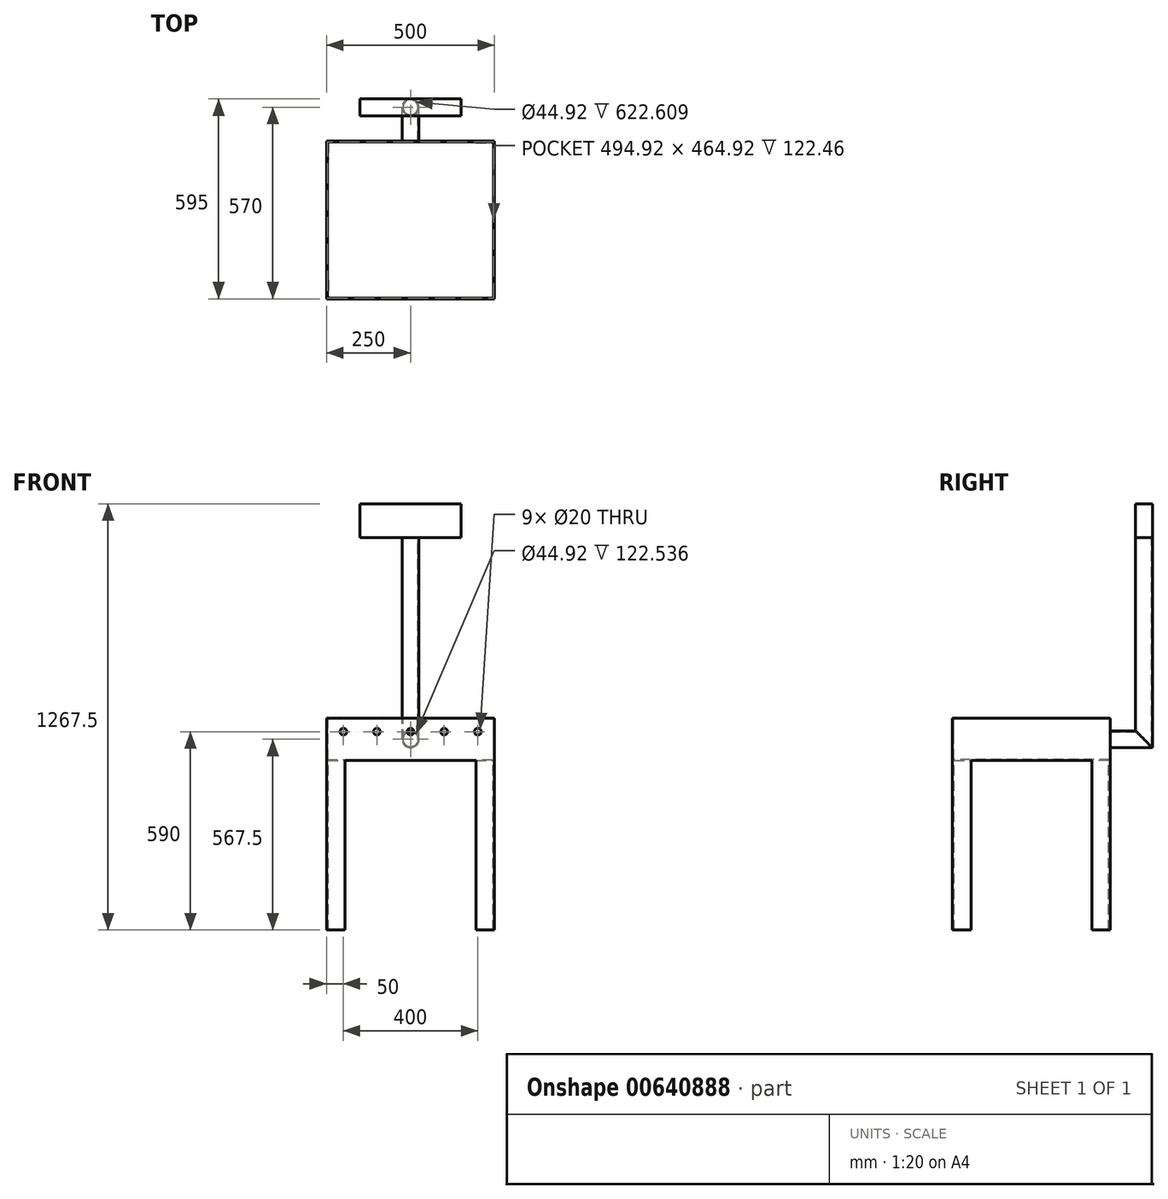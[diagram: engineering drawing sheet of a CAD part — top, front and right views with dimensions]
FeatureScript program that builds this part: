
annotation { "Feature Type Name" : "Feature", "Feature Type Description" : "" }
export const myFeature = defineFeature(function(context is Context, id is Id, definition is map)
    precondition{}
    {
        {
            var Q0;
            Q0=qCreatedBy(makeId("Top.planeOp"),FACE);
            var sketch = newSketch(context, id + "F0", { "sketchPlane" : qUnion([Q0])});
            skLineSegment(sketch, "E0", {"start": v(0, 238.63) * mm, "end": v(0, -211.4) * mm, "construction": true});
            skLineSegment(sketch, "E1", {"start": v(-197.8, 0) * mm, "end": v(217.76, 0) * mm, "construction": true});
            skLineSegment(sketch, "E2.bottom", {"start": v(-250, 235) * mm, "end": v(250, 235) * mm});
            skLineSegment(sketch, "E2.top", {"start": v(-250, -235) * mm, "end": v(250, -235) * mm});
            skLineSegment(sketch, "E2.left", {"start": v(-250, 235) * mm, "end": v(-250, -235) * mm});
            skLineSegment(sketch, "E2.right", {"start": v(250, 235) * mm, "end": v(250, -235) * mm});
            skSolve(sketch);
        }
        {
            var Q0;
            Q0 = qSketchRegion(id + "F0", true);
            extrude(context, id + "F1", {"entities" : qUnion([Q0]), "depth" : 125 * mm, "offsetDistance" : 25.4 * mm});
        }
        {
            var Q0;
            Q0=makeQuery(id+"F1.opExtrude","CAP_FACE",FACE,{"disambiguationData":[OSD([sQuery(id+"F0.wireOp",EDGE,"E2.bottom"),sQuery(id+"F0.wireOp",EDGE,"E2.top"),sQuery(id+"F0.wireOp",EDGE,"E2.left"),sQuery(id+"F0.wireOp",EDGE,"E2.right")])],"isStart":false});
            shell(context, id + "F2", {"entities" : qUnion([Q0]), "thickness" : 2.54 * mm});
        }
        {
            var Q0;
            Q0=makeQuery(id+"F1.opExtrude","SWEPT_FACE",FACE,{"disambiguationData":[OSD([sQuery(id+"F0.wireOp",EDGE,"E2.bottom")])]});
            var sketch = newSketch(context, id + "F3", { "sketchPlane" : qUnion([Q0])});
            skLineSegment(sketch, "E3", {"start": v(0, 125) * mm, "end": v(0, 0) * mm, "construction": true});
            skLineSegment(sketch, "E4", {"start": v(-250, 62.5) * mm, "end": v(250, 62.5) * mm, "construction": true});
            skCircle(sketch, "E5", {"center": v(0, 62.5) * mm, "radius": 25 * mm});
            skSolve(sketch);
        }
        {
            var Q0;
            Q0=makeQuery(id+"F1.opExtrude","SWEPT_FACE",FACE,{"disambiguationData":[OSD([sQuery(id+"F0.wireOp",EDGE,"E2.right")])]});
            var Q1;
            Q1=sQuery(id+"F3.wireOp",VERTEX,"E5.center");
            cPlane(context, id + "F4", {"entities" : qUnion([Q0, Q1]), "cplaneType" : CPlaneType.PLANE_POINT, "offset" : 25.4 * mm, "width" : 152.4 * mm, "height" : 152.4 * mm});
        }
        {
            var Q0;
            Q0=qCreatedBy(id+"F4.planeOp",FACE);
            var sketch = newSketch(context, id + "F5", { "sketchPlane" : qUnion([Q0])});
            skLineSegment(sketch, "E6", {"start": v(235, 62.5) * mm, "end": v(335, 62.5) * mm});
            skLineSegment(sketch, "E7", {"start": v(335, 62.5) * mm, "end": v(335, 662.5) * mm});
            skSolve(sketch);
        }
        {
            var Q0;
            Q0=makeQuery(id+"F3.imprint","IMPRINT",FACE,{"disambiguationData":[TD([[makeQuery(id+"F3.imprint","IMPRINT",EDGE,{"derivedFrom":sQuery(id+"F3.wireOp",EDGE,"E5")}),1.0]])]});
            var Q1;
            Q1=sQuery(id+"F5.wireOp",EDGE,"E6");
            var Q2;
            Q2=sQuery(id+"F5.wireOp",EDGE,"E7");
            sweep(context, id + "F6", {"operationType" : NewBodyOperationType.ADD, "profiles" : qUnion([Q0]), "path" : qUnion([Q1, Q2])});
        }
        {
            var Q0;
            Q0=makeQuery(id+"F6.opSweep","CAP_FACE",FACE,{"disambiguationData":[OSD([sQuery(id+"F3.wireOp",EDGE,"E5"),sQuery(id+"F5.wireOp",VERTEX,"E7.end")])],"isStart":false});
            shell(context, id + "F7", {"entities" : qUnion([Q0]), "thickness" : 2.54 * mm});
        }
        {
            var Q0;
            Q0=makeQuery(id+"F6.opSweep","CAP_FACE",FACE,{"disambiguationData":[OSD([sQuery(id+"F3.wireOp",EDGE,"E5"),sQuery(id+"F5.wireOp",VERTEX,"E7.end")])],"isStart":false});
            var sketch = newSketch(context, id + "F8", { "sketchPlane" : qUnion([Q0])});
            skLineSegment(sketch, "E8.bottom", {"start": v(-150, 360) * mm, "end": v(150, 360) * mm});
            skLineSegment(sketch, "E8.top", {"start": v(-150, 310) * mm, "end": v(150, 310) * mm});
            skLineSegment(sketch, "E8.left", {"start": v(-150, 360) * mm, "end": v(-150, 310) * mm});
            skLineSegment(sketch, "E8.right", {"start": v(150, 360) * mm, "end": v(150, 310) * mm});
            skLineSegment(sketch, "E9", {"start": v(0, 372.77) * mm, "end": v(0, 297.23) * mm, "construction": true});
            skPoint(sketch, "E10.startSnap0", {"position": v(0, 335) * mm});
            skLineSegment(sketch, "E11", {"start": v(-99.69, 335) * mm, "end": v(99.79, 335) * mm, "construction": true});
            skCircle(sketch, "E12", {"center": v(0, 335) * mm, "radius": 25 * mm, "construction": true});
            skSolve(sketch);
        }
        {
            var Q0;
            {var subQ0=sQuery(id+"F8.wireOp",EDGE,"E8.left");Q0=makeQuery(id+"F8.imprint","IMPRINT",FACE,{"disambiguationData":[TD([[makeQuery(id+"F8.imprint","IMPRINT",EDGE,{"derivedFrom":subQ0}),1.0]])]});}
            var Q1;
            Q1 = qSketchRegion(id + "F8", true);
            extrude(context, id + "F9", {"entities" : qUnion([Q0, Q1]), "operationType" : NewBodyOperationType.ADD, "depth" : 100 * mm, "offsetDistance" : 25.4 * mm});
        }
        {
            var Q0;
            Q0=makeQuery(id+"F1.opExtrude","SWEPT_FACE",FACE,{"disambiguationData":[OSD([sQuery(id+"F0.wireOp",EDGE,"E2.top")])]});
            var sketch = newSketch(context, id + "F10", { "sketchPlane" : qUnion([Q0])});
            skLineSegment(sketch, "E13", {"start": v(-250, 85) * mm, "end": v(250, 85) * mm, "construction": true});
            skCircle(sketch, "E14", {"center": v(-200, 85) * mm, "radius": 10 * mm});
            skCircle(sketch, "E15.1.0.0", {"center": v(-100, 85) * mm, "radius": 10 * mm});
            skCircle(sketch, "E15.2.0.0", {"center": v(0, 85) * mm, "radius": 10 * mm});
            skCircle(sketch, "E15.3.0.0", {"center": v(100, 85) * mm, "radius": 10 * mm});
            skCircle(sketch, "E15.4.0.0", {"center": v(200, 85) * mm, "radius": 10 * mm});
            skLineSegment(sketch, "E15.direction1", {"start": v(-200, 85) * mm, "end": v(-100, 85) * mm, "construction": true});
            skCircle(sketch, "E16.0.5.0", {"center": v(300, 85) * mm, "radius": 10 * mm});
            skCircle(sketch, "E16.0.6.0", {"center": v(400, 85) * mm, "radius": 10 * mm});
            skCircle(sketch, "E16.0.7.0", {"center": v(500, 85) * mm, "radius": 10 * mm});
            skCircle(sketch, "E16.0.8.0", {"center": v(600, 85) * mm, "radius": 10 * mm});
            skCircle(sketch, "E16.0.9.0", {"center": v(700, 85) * mm, "radius": 10 * mm});
            skSolve(sketch);
        }
        {
            var Q0;
            Q0 = qSketchRegion(id + "F10", true);
            var Q1;
            Q1=makeQuery(id+"F1.opExtrude","SWEPT_FACE",FACE,{"disambiguationData":[OSD([sQuery(id+"F0.wireOp",EDGE,"E2.bottom")])]});
            extrude(context, id + "F11", {"entities" : qUnion([Q0]), "operationType" : NewBodyOperationType.REMOVE, "endBound" : BoundingType.UP_TO_SURFACE, "oppositeDirection" : true, "depth" : 25.4 * mm, "endBoundEntityFace" : qUnion([Q1]), "offsetDistance" : 25.4 * mm});
        }
        {
            var Q0;
            Q0=makeQuery(id+"F1.opExtrude","CAP_FACE",FACE,{"disambiguationData":[OSD([sQuery(id+"F0.wireOp",EDGE,"E2.bottom"),sQuery(id+"F0.wireOp",EDGE,"E2.top"),sQuery(id+"F0.wireOp",EDGE,"E2.left"),sQuery(id+"F0.wireOp",EDGE,"E2.right")])],"isStart":true});
            var sketch = newSketch(context, id + "F12", { "sketchPlane" : qUnion([Q0])});
            skLineSegment(sketch, "E17", {"start": v(-195, 235) * mm, "end": v(-250, 235) * mm});
            skLineSegment(sketch, "E18", {"start": v(-250, 235) * mm, "end": v(-250, 180) * mm});
            skLineSegment(sketch, "E19", {"start": v(-250, 180) * mm, "end": v(-245, 180) * mm});
            skLineSegment(sketch, "E20", {"start": v(-245, 180) * mm, "end": v(-245, 230) * mm});
            skLineSegment(sketch, "E21", {"start": v(-245, 230) * mm, "end": v(-195, 230) * mm});
            skLineSegment(sketch, "E22", {"start": v(-195, 230) * mm, "end": v(-195, 235) * mm});
            skLineSegment(sketch, "E23", {"start": v(-250, -235) * mm, "end": v(-250, -180) * mm});
            skLineSegment(sketch, "E24", {"start": v(-250, -235) * mm, "end": v(-195, -235) * mm});
            skLineSegment(sketch, "E25", {"start": v(-195, -235) * mm, "end": v(-195, -230) * mm});
            skLineSegment(sketch, "E26", {"start": v(-195, -230) * mm, "end": v(-245, -230) * mm});
            skLineSegment(sketch, "E27", {"start": v(-245, -230) * mm, "end": v(-245, -180) * mm});
            skLineSegment(sketch, "E28", {"start": v(-245, -180) * mm, "end": v(-250, -180) * mm});
            skLineSegment(sketch, "E29", {"start": v(250, -180) * mm, "end": v(250, -235) * mm});
            skLineSegment(sketch, "E30", {"start": v(250, -235) * mm, "end": v(195, -235) * mm});
            skLineSegment(sketch, "E31", {"start": v(195, -235) * mm, "end": v(195, -230) * mm});
            skLineSegment(sketch, "E32", {"start": v(195, -230) * mm, "end": v(245, -230) * mm});
            skLineSegment(sketch, "E33", {"start": v(245, -230) * mm, "end": v(245, -180) * mm});
            skLineSegment(sketch, "E34", {"start": v(245, -180) * mm, "end": v(250, -180) * mm});
            skLineSegment(sketch, "E35", {"start": v(250, 235) * mm, "end": v(195, 235) * mm});
            skLineSegment(sketch, "E36", {"start": v(195, 235) * mm, "end": v(195, 230) * mm});
            skLineSegment(sketch, "E37", {"start": v(195, 230) * mm, "end": v(245, 230) * mm});
            skLineSegment(sketch, "E38", {"start": v(245, 230) * mm, "end": v(245, 180) * mm});
            skLineSegment(sketch, "E39", {"start": v(245, 180) * mm, "end": v(250, 180) * mm});
            skLineSegment(sketch, "E40", {"start": v(250, 180) * mm, "end": v(250, 235) * mm});
            skSolve(sketch);
        }
        {
            var Q0;
            Q0 = qSketchRegion(id + "F12", true);
            extrude(context, id + "F13", {"entities" : qUnion([Q0]), "operationType" : NewBodyOperationType.ADD, "depth" : 505 * mm, "offsetDistance" : 25.4 * mm});
        }
    });
